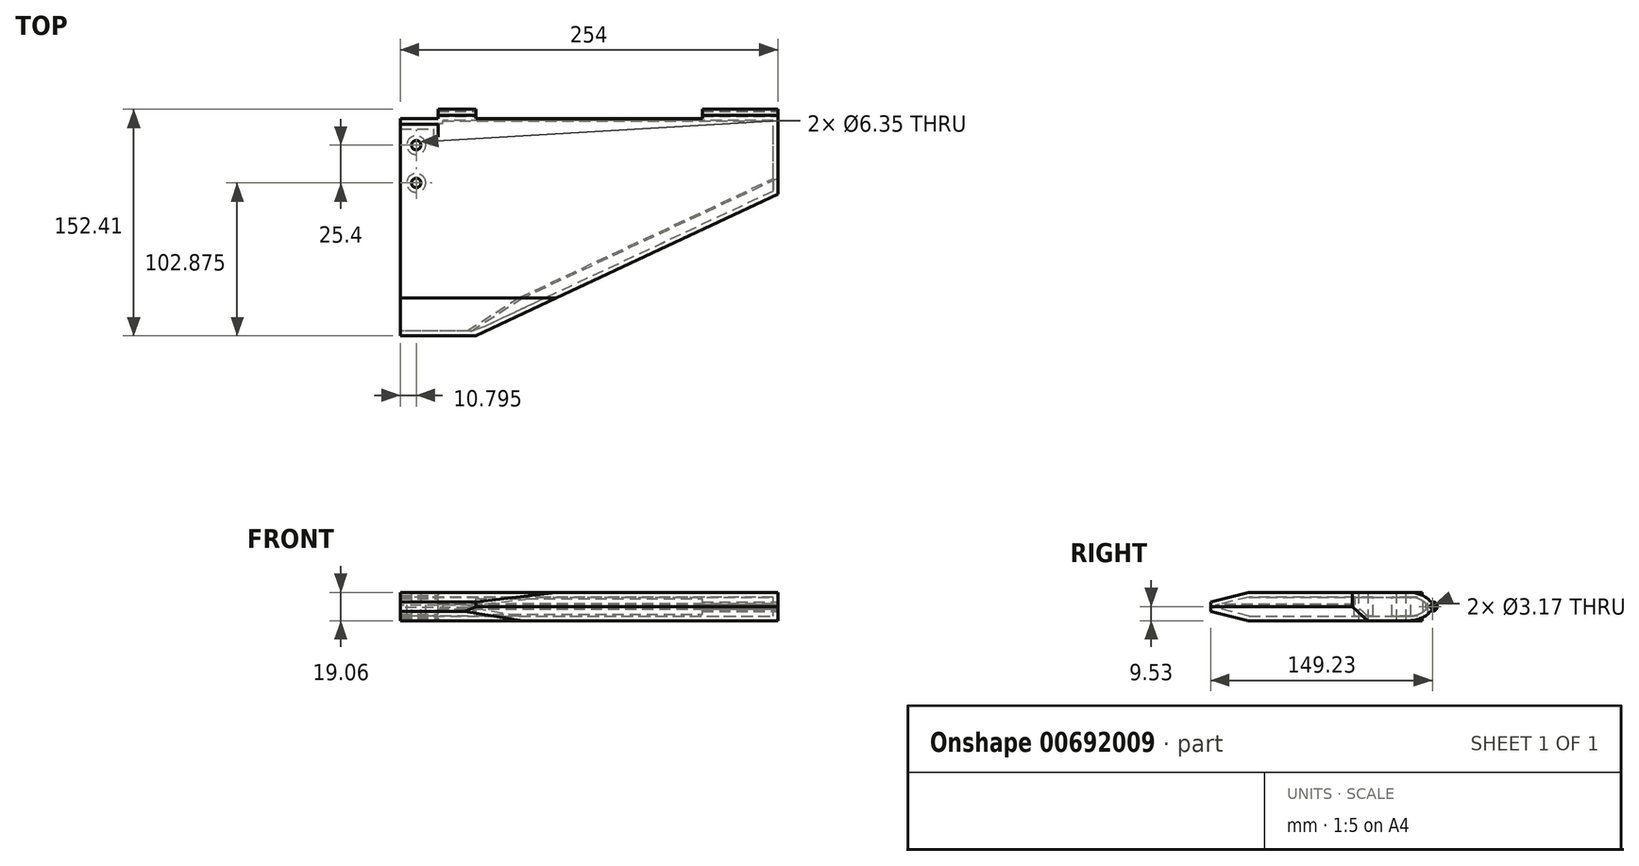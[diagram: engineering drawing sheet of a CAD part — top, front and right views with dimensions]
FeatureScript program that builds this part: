
annotation { "Feature Type Name" : "Feature", "Feature Type Description" : "" }
export const myFeature = defineFeature(function(context is Context, id is Id, definition is map)
    precondition{}
    {
        {
            var Q0;
            Q0=qCreatedBy(makeId("Right.planeOp"),FACE);
            var sketch = newSketch(context, id + "F0", { "sketchPlane" : qUnion([Q0])});
            skLineSegment(sketch, "E0.bottom", {"start": v(-73.03, 9.53) * mm, "end": v(73.03, 9.53) * mm});
            skLineSegment(sketch, "E0.top", {"start": v(-73.03, -9.53) * mm, "end": v(73.03, -9.53) * mm});
            skLineSegment(sketch, "E0.left", {"start": v(-73.03, 9.53) * mm, "end": v(-73.03, -9.53) * mm});
            skLineSegment(sketch, "E0.right", {"start": v(73.03, 9.53) * mm, "end": v(73.03, -9.53) * mm});
            skPoint(sketch, "E0.middle", {"position": v(0, 0) * mm});
            skLineSegment(sketch, "E1", {"start": v(-73.03, -9.53) * mm, "end": v(-73.03, -6.35) * mm});
            skLineSegment(sketch, "E2", {"start": v(-73.03, 9.53) * mm, "end": v(-73.03, 6.35) * mm});
            skLineSegment(sketch, "E3", {"start": v(-73.03, 9.53) * mm, "end": v(-47.62, 9.53) * mm});
            skLineSegment(sketch, "E4", {"start": v(-47.62, 9.53) * mm, "end": v(-47.62, -9.53) * mm});
            skLineSegment(sketch, "E5", {"start": v(-73.03, 0) * mm, "end": v(-73.03, -3.18) * mm});
            skLineSegment(sketch, "E6", {"start": v(-73.03, -3.18) * mm, "end": v(-73.03, 3.17) * mm});
            skLineSegment(sketch, "E7", {"start": v(-47.62, 9.53) * mm, "end": v(-73.03, 3.17) * mm});
            skLineSegment(sketch, "E8", {"start": v(-47.62, -9.53) * mm, "end": v(-73.03, -3.18) * mm});
            skSolve(sketch);
        }
        {
            var Q0;
            Q0 = qSketchRegion(id + "F0", true);
            extrude(context, id + "F1", {"entities" : qUnion([Q0]), "depth" : 254 * mm, "offsetDistance" : 25.4 * mm});
        }
        {
            var Q0;
            Q0=makeQuery(id+"F1.opExtrude","SWEPT_FACE",FACE,{"disambiguationData":[OSD([sQuery(id+"F0.wireOp",EDGE,"E0.bottom")])]});
            var sketch = newSketch(context, id + "F2", { "sketchPlane" : qUnion([Q0])});
            skLineSegment(sketch, "E9", {"start": v(0, -73.03) * mm, "end": v(50.8, -73.03) * mm});
            skLineSegment(sketch, "E10", {"start": v(254, 73.03) * mm, "end": v(254, 22.22) * mm});
            skLineSegment(sketch, "E11", {"start": v(254, 22.23) * mm, "end": v(50.8, -73.03) * mm});
            skLineSegment(sketch, "E12", {"start": v(0, 73.03) * mm, "end": v(0, 73.03) * mm});
            skLineSegment(sketch, "E13", {"start": v(0, 73.03) * mm, "end": v(0, 55.25) * mm});
            skLineSegment(sketch, "E14", {"start": v(0, 55.25) * mm, "end": v(10.8, 55.25) * mm});
            skLineSegment(sketch, "E15", {"start": v(10.8, 55.25) * mm, "end": v(10.8, 29.84) * mm});
            skCircle(sketch, "E16", {"center": v(10.8, 55.25) * mm, "radius": 3.18 * mm});
            skCircle(sketch, "E17", {"center": v(10.8, 29.84) * mm, "radius": 3.18 * mm});
            skSolve(sketch);
        }
        {
            var Q0;
            Q0 = qSketchRegion(id + "F2", true);
            var Q1;
            {var subQ0=sQuery(id+"F2.wireOp",EDGE,"E11");Q1=makeQuery(id+"F2.imprint","IMPRINT",FACE,{"disambiguationData":[TD([[makeQuery(id+"F2.imprint","IMPRINT",EDGE,{"derivedFrom":subQ0}),1.0]])]});}
            extrude(context, id + "F3", {"entities" : qUnion([Q0, Q1]), "operationType" : NewBodyOperationType.REMOVE, "endBound" : BoundingType.THROUGH_ALL, "oppositeDirection" : true, "depth" : 25.4 * mm, "offsetDistance" : 25.4 * mm});
        }
        {
            var Q0;
            Q0=makeQuery(id+"F3.boolean.opBoolean","COPY",EDGE,{"derivedFrom":makeQuery(id+"F3.opExtrude","CAP_EDGE",EDGE,{"disambiguationData":[OSD([sQuery(id+"F2.wireOp",EDGE,"E11")])],"isStart":true})});
            var Q1;
            Q1=makeQuery(id+"F3.boolean.opBoolean","INTERSECT",EDGE,{"derivedFrom":[makeQuery(id+"F1.opExtrude","SWEPT_FACE",FACE,{"disambiguationData":[OSD([sQuery(id+"F0.wireOp",EDGE,"E0.top")])]}),makeQuery(id+"F3.opExtrude","SWEPT_FACE",FACE,{"disambiguationData":[OSD([sQuery(id+"F2.wireOp",EDGE,"E11")])]})]});
            chamfer(context, id + "F4", {"entities" : qUnion([Q0, Q1]), "width" : 9.52 * mm, "tangentPropagation" : true});
        }
        {
            var Q0;
            {var subQ0=sQuery(id+"F0.wireOp",EDGE,"HUjc3N7K-iRee-XVtz-STow-2uoOrDmlqWwK");Q0=makeQuery(id+"F0.imprint","IMPRINT",FACE,{"disambiguationData":[TD([[makeQuery(id+"F0.imprint","IMPRINT",EDGE,{"derivedFrom":subQ0}),1.0]])]});}
            var Q1;
            {var subQ0=sQuery(id+"F0.wireOp",EDGE,"Glp7gCq1-iR8m-ocv8-P6zi-vuiqfP8sHICv");Q1=makeQuery(id+"F0.imprint","IMPRINT",FACE,{"disambiguationData":[TD([[makeQuery(id+"F0.imprint","IMPRINT",EDGE,{"derivedFrom":subQ0}),1.0]])]});}
            var Q2;
            {var subQ0=sQuery(id+"F0.wireOp",EDGE,"E7");Q2=makeQuery(id+"F0.imprint","IMPRINT",FACE,{"disambiguationData":[TD([[makeQuery(id+"F0.imprint","IMPRINT",EDGE,{"derivedFrom":subQ0}),-1.0]])]});}
            var Q3;
            {var subQ0=sQuery(id+"F0.wireOp",EDGE,"E8");Q3=makeQuery(id+"F0.imprint","IMPRINT",FACE,{"disambiguationData":[TD([[makeQuery(id+"F0.imprint","IMPRINT",EDGE,{"derivedFrom":subQ0}),1.0]])]});}
            extrude(context, id + "F5", {"entities" : qUnion([Q0, Q1, Q2, Q3]), "operationType" : NewBodyOperationType.REMOVE, "endBound" : BoundingType.THROUGH_ALL, "depth" : 25.4 * mm, "offsetDistance" : 25.4 * mm});
        }
        {
            var Q0;
            Q0=makeQuery(id+"F1.opExtrude","CAP_FACE",FACE,{"disambiguationData":[OSD([sQuery(id+"F0.wireOp",EDGE,"E0.bottom"),sQuery(id+"F0.wireOp",EDGE,"E0.top"),sQuery(id+"F0.wireOp",EDGE,"E0.left"),sQuery(id+"F0.wireOp",EDGE,"E0.right")])],"isStart":false});
            var sketch = newSketch(context, id + "F6", { "sketchPlane" : qUnion([Q0])});
            skLineSegment(sketch, "E18", {"start": v(73.03, 9.53) * mm, "end": v(73.03, 0) * mm});
            skLineSegment(sketch, "E19", {"start": v(73.03, 0) * mm, "end": v(76.2, 0) * mm});
            skLineSegment(sketch, "E20", {"start": v(76.2, 0) * mm, "end": v(73.02, 9.53) * mm});
            skLineSegment(sketch, "E21", {"start": v(73.03, -9.53) * mm, "end": v(76.2, 0) * mm});
            skCircle(sketch, "E22", {"center": v(76.2, 0) * mm, "radius": 3.18 * mm});
            skCircle(sketch, "E23", {"center": v(76.2, 0) * mm, "radius": 1.59 * mm});
            skSolve(sketch);
        }
        {
            var Q0;
            Q0 = qSketchRegion(id + "F6", true);
            var Q1;
            {var subQ0=sQuery(id+"F6.wireOp",EDGE,"E21");var subQ3=sQuery(id+"F6.wireOp",EDGE,"E22");var subQ4=makeQuery(id+"F6.imprint","INTERSECT",VERTEX,{"derivedFrom":[subQ0,subQ3]});Q1=makeQuery(id+"F6.imprint","IMPRINT",FACE,{"disambiguationData":[TD([[makeQuery(id+"F6.imprint","IMPRINT",EDGE,{"disambiguationData":[TD([[subQ4,1.0]])],"derivedFrom":subQ0}),1.0]])]});}
            extrude(context, id + "F7", {"entities" : qUnion([Q0, Q1]), "operationType" : NewBodyOperationType.ADD, "oppositeDirection" : true, "depth" : 254 * mm, "offsetDistance" : 25.4 * mm});
        }
        {
            var Q0;
            Q0=makeQuery(id+"F1.opExtrude","SWEPT_FACE",FACE,{"disambiguationData":[OSD([sQuery(id+"F0.wireOp",EDGE,"E0.bottom")])]});
            var sketch = newSketch(context, id + "F8", { "sketchPlane" : qUnion([Q0])});
            skLineSegment(sketch, "E24", {"start": v(0, 73.03) * mm, "end": v(50.8, 73.03) * mm});
            skLineSegment(sketch, "E25", {"start": v(50.8, 73.03) * mm, "end": v(203.2, 73.03) * mm});
            skLineSegment(sketch, "E26.top", {"start": v(50.8, 123.83) * mm, "end": v(203.2, 123.83) * mm});
            skLineSegment(sketch, "E26.left", {"start": v(50.8, 73.03) * mm, "end": v(50.8, 123.83) * mm});
            skLineSegment(sketch, "E26.right", {"start": v(203.2, 73.03) * mm, "end": v(203.2, 123.83) * mm});
            skSolve(sketch);
        }
        {
            var Q0;
            {var subQ0=sQuery(id+"F6.wireOp",EDGE,"E20");var subQ1=sQuery(id+"F0.wireOp",EDGE,"E0.right");var subQ2=sQuery(id+"F0.wireOp",EDGE,"E0.bottom");var subQ3=sQuery(id+"F6.wireOp",EDGE,"E18");Q0=makeQuery(id+"F0xAijl7oDghpIc_1.boolean.opBoolean","SPLIT",EDGE,{"disambiguationData":[TD([makeQuery(id+"F0xAijl7oDghpIc_1.opExtrude","SWEPT_FACE",FACE,{"disambiguationData":[OSD([sQuery(id+"Fa5dQilrRDUwoAG_1.wireOp",EDGE,"AknoTKYk-zPv5-nR07-hBEs-5b61587hsY2X")])]})])],"derivedFrom":makeQuery(id+"F7.boolean.opBoolean","MERGE",EDGE,{"derivedFrom":[makeQuery(id+"F1.opExtrude","SWEPT_EDGE",EDGE,{"disambiguationData":[OSD([subQ2,subQ1])]}),makeQuery(id+"F7.opExtrude","SWEPT_EDGE",EDGE,{"disambiguationData":[OSD([subQ2,subQ3,subQ0])]})]})});}
            var Q1;
            {var subQ0=sQuery(id+"F6.wireOp",EDGE,"E21");var subQ1=makeQuery(id+"F7.opExtrude","SWEPT_FACE",FACE,{"disambiguationData":[OSD([subQ0])]});var subQ2=sQuery(id+"F0.wireOp",EDGE,"E0.right");var subQ3=sQuery(id+"F0.wireOp",EDGE,"E0.top");var subQ4=makeQuery(id+"F1.opExtrude","SWEPT_FACE",FACE,{"disambiguationData":[OSD([subQ3])]});Q1=makeQuery(id+"F0xAijl7oDghpIc_1.boolean.opBoolean","SPLIT",EDGE,{"disambiguationData":[topologyDisambiguationEdgeConnected([subQ4,subQ1]),TD([makeQuery(id+"F0xAijl7oDghpIc_1.opExtrude","SWEPT_FACE",FACE,{"disambiguationData":[OSD([sQuery(id+"Fa5dQilrRDUwoAG_1.wireOp",EDGE,"AknoTKYk-zPv5-nR07-hBEs-5b61587hsY2X")])]})])],"derivedFrom":makeQuery(id+"F7.boolean.opBoolean","MERGE",EDGE,{"derivedFrom":[makeQuery(id+"F1.opExtrude","SWEPT_EDGE",EDGE,{"disambiguationData":[OSD([subQ3,subQ2])]}),makeQuery(id+"F7.opExtrude","SWEPT_EDGE",EDGE,{"disambiguationData":[OSD([subQ3,subQ2,subQ0])]})]})});}
            fillet(context, id + "F9", {"entities" : qUnion([Q0, Q1]), "tangentPropagation" : true, "radius" : 19.05 * mm, "defaultsChanged" : true, "vertexSettings" : [], "allowEdgeOverflow" : false});
        }
        {
            var Q0;
            Q0=makeQuery(id+"F1.opExtrude","SWEPT_FACE",FACE,{"disambiguationData":[OSD([sQuery(id+"F0.wireOp",EDGE,"E0.bottom")])]});
            var sketch = newSketch(context, id + "F10", { "sketchPlane" : qUnion([Q0])});
            skLineSegment(sketch, "E27.bottom", {"start": v(0, -73.03) * mm, "end": v(0, -73.03) * mm});
            skLineSegment(sketch, "E27.top", {"start": v(0, 73.03) * mm, "end": v(0, 73.03) * mm});
            skLineSegment(sketch, "E27.left", {"start": v(0, -73.03) * mm, "end": v(0, 73.03) * mm});
            skLineSegment(sketch, "E27.right", {"start": v(0, -73.03) * mm, "end": v(0, 73.03) * mm});
            skPoint(sketch, "E27.middle", {"position": v(0, 0) * mm});
            skLineSegment(sketch, "E28", {"start": v(0, 73.03) * mm, "end": v(25.4, 73.03) * mm});
            skLineSegment(sketch, "E29", {"start": v(25.4, 73.03) * mm, "end": v(25.4, 90.49) * mm});
            skLineSegment(sketch, "E30", {"start": v(25.4, 90.49) * mm, "end": v(0, 90.49) * mm});
            skLineSegment(sketch, "E31", {"start": v(0, 90.49) * mm, "end": v(0, 73.03) * mm});
            skLineSegment(sketch, "E32", {"start": v(25.4, 73.03) * mm, "end": v(25.4, 60.85) * mm});
            skLineSegment(sketch, "E33", {"start": v(25.4, 60.85) * mm, "end": v(0, 60.85) * mm});
            skLineSegment(sketch, "E34", {"start": v(0, -73.03) * mm, "end": v(0, 69.22) * mm});
            skLineSegment(sketch, "E35", {"start": v(0, 69.22) * mm, "end": v(25.4, 69.22) * mm});
            skLineSegment(sketch, "E36", {"start": v(0, 69.22) * mm, "end": v(0, 55.24) * mm});
            skLineSegment(sketch, "E37", {"start": v(0, 55.24) * mm, "end": v(6.35, 55.24) * mm});
            skCircle(sketch, "E38", {"center": v(6.35, 55.24) * mm, "radius": 1.59 * mm});
            skLineSegment(sketch, "E39", {"start": v(6.35, 55.24) * mm, "end": v(6.35, 29.84) * mm});
            skCircle(sketch, "E40", {"center": v(6.35, 29.84) * mm, "radius": 1.59 * mm});
            skSolve(sketch);
        }
        {
            var Q0;
            Q0=makeQuery(id+"F10.imprint","IMPRINT",FACE,{"disambiguationData":[TD([[makeQuery(id+"F10.imprint","IMPRINT",EDGE,{"derivedFrom":sQuery(id+"F10.wireOp",EDGE,"E28")}),1.0]])]});
            var Q1;
            Q1=makeQuery(id+"F10.imprint","IMPRINT",FACE,{"disambiguationData":[TD([[makeQuery(id+"F10.imprint","IMPRINT",EDGE,{"derivedFrom":sQuery(id+"F10.wireOp",EDGE,"E27.right")}),-1.0]])]});
            extrude(context, id + "F11", {"entities" : qUnion([Q0, Q1]), "operationType" : NewBodyOperationType.REMOVE, "endBound" : BoundingType.THROUGH_ALL, "oppositeDirection" : true, "depth" : 25.4 * mm, "offsetDistance" : 25.4 * mm});
        }
        {
            var Q0;
            {var subQ0=sQuery(id+"F10.wireOp",EDGE,"E33");Q0=makeQuery(id+"F10.imprint","IMPRINT",FACE,{"disambiguationData":[TD([[makeQuery(id+"F10.imprint","IMPRINT",EDGE,{"derivedFrom":subQ0}),-1.0]])]});}
            extrude(context, id + "F12", {"entities" : qUnion([Q0]), "operationType" : NewBodyOperationType.ADD, "oppositeDirection" : true, "depth" : 19.05 * mm, "offsetDistance" : 25.4 * mm});
        }
        {
            var Q0;
            {var subQ0=sQuery(id+"F0.wireOp",EDGE,"E0.right");Q0=makeQuery(id+"F7.boolean.opBoolean","MERGE",FACE,{"derivedFrom":[makeQuery(id+"F1.opExtrude","CAP_FACE",FACE,{"disambiguationData":[OSD([sQuery(id+"F0.wireOp",EDGE,"E0.bottom"),sQuery(id+"F0.wireOp",EDGE,"E0.top"),sQuery(id+"F0.wireOp",EDGE,"E0.left"),subQ0])],"isStart":true}),makeQuery(id+"F7.opExtrude","CAP_FACE",FACE,{"disambiguationData":[OSD([subQ0,sQuery(id+"F6.wireOp",EDGE,"E18"),sQuery(id+"F6.wireOp",EDGE,"E20"),sQuery(id+"F6.wireOp",EDGE,"E21"),sQuery(id+"F6.wireOp",EDGE,"E22"),sQuery(id+"F6.wireOp",EDGE,"E23")])],"isStart":false})]});}
            shell(context, id + "F13", {"entities" : qUnion([Q0]), "thickness" : 3.17 * mm});
        }
        {
            var Q0;
            Q0=makeQuery(id+"F8.imprint","IMPRINT",FACE,{"disambiguationData":[TD([[makeQuery(id+"F8.imprint","IMPRINT",EDGE,{"derivedFrom":sQuery(id+"F8.wireOp",EDGE,"E25")}),-1.0]])]});
            extrude(context, id + "F14", {"entities" : qUnion([Q0]), "operationType" : NewBodyOperationType.REMOVE, "endBound" : BoundingType.THROUGH_ALL, "oppositeDirection" : true, "depth" : 25.4 * mm, "offsetDistance" : 25.4 * mm});
        }
        {
            var Q0;
            Q0 = qSketchRegion(id + "F2", true);
            extrude(context, id + "F15", {"entities" : qUnion([Q0]), "operationType" : NewBodyOperationType.REMOVE, "endBound" : BoundingType.THROUGH_ALL, "oppositeDirection" : true, "depth" : 25.4 * mm, "offsetDistance" : 25.4 * mm});
        }
    });
